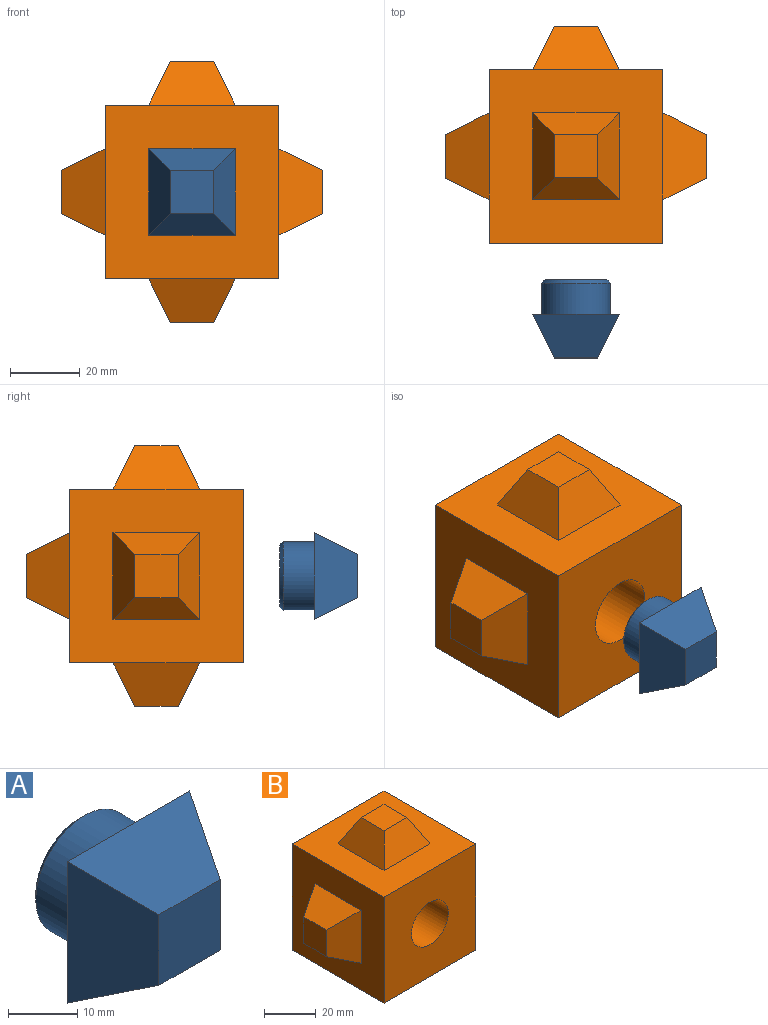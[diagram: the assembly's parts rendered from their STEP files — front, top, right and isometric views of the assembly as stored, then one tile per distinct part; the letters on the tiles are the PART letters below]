
ASSEMBLY  parts=2 mates=1
PART A: 16 faces, bbox 25x22.5x25 mm
  f0: plane 25x25mm, normal (0,1,0), area 317.1mm2, adj f2,f3,f4,f5,f6
  f1: plane 12.5x12.5mm, normal (0,-1,0), area 156.3mm2, adj f2,f3,f4,f5
  f2: plane 25x12.5mm, normal (0,-0.45,-0.89), area 262mm2, adj f0,f1,f3,f5
  f3: plane 25x12.5mm, normal (0.89,-0.45,0), area 262mm2, adj f0,f1,f2,f4
  f4: plane 25x12.5mm, normal (0,-0.45,0.89), area 262mm2, adj f0,f1,f3,f5
  f5: plane 25x12.5mm, normal (-0.89,-0.45,0), area 262mm2, adj f0,f1,f2,f4
  f6: cylinder r=9.9mm len=19.8mm, axis (0,-1,0), area 559.8mm2, adj f0,f15
  f7: plane 17.8x17.8mm, normal (0,1,0), area 76.8mm2, adj f14,f15
  f8: plane 16.91x16.91mm, normal (0,-1,0), area 113.9mm2, adj f10,f11,f12,f13,f14
  f9: plane 9.41x9.41mm, normal (0,1,0), area 88.5mm2, adj f10,f11,f12,f13
  f10: plane 16.91x7.5mm, normal (0,0.45,0.89), area 110.3mm2, adj f8,f9,f11,f13
  f11: plane 16.91x7.5mm, normal (-0.89,0.45,0), area 110.3mm2, adj f8,f9,f10,f12
  f12: plane 16.91x7.5mm, normal (0,0.45,-0.89), area 110.3mm2, adj f8,f9,f11,f13
  f13: plane 16.91x7.5mm, normal (0.89,0.45,0), area 110.3mm2, adj f8,f9,f10,f12
  f14: cylinder r=7.4mm len=14.8mm, axis (0,-1,0), area 581.2mm2, adj f7,f8
  f15: cone r=8.9mm half-angle=45deg, axis (0,-1,0), area 83.5mm2, adj f6,f7
PART B: 33 faces, bbox 75x62.5x75 mm
  f0: plane 12.5x12.5mm, normal (-1,0,0), area 156.3mm2, adj f1,f2,f3,f4
  f1: plane 25x12.5mm, normal (-0.45,0,-0.89), area 262mm2, adj f0,f2,f4,f13
  f2: plane 25x12.5mm, normal (-0.45,-0.89,0), area 262mm2, adj f0,f1,f3,f13
  f3: plane 25x12.5mm, normal (-0.45,0,0.89), area 262mm2, adj f0,f2,f4,f13
  f4: plane 25x12.5mm, normal (-0.45,0.89,0), area 262mm2, adj f0,f1,f3,f13
  f5: plane 12.5x12.5mm, normal (0,0,1), area 156.3mm2, adj f6,f7,f8,f9
  f6: plane 25x12.5mm, normal (-0.89,0,0.45), area 262mm2, adj f5,f7,f9,f12
  f7: plane 25x12.5mm, normal (0,-0.89,0.45), area 262mm2, adj f5,f6,f8,f12
  f8: plane 25x12.5mm, normal (0.89,0,0.45), area 262mm2, adj f5,f7,f9,f12
  f9: plane 25x12.5mm, normal (0,0.89,0.45), area 262mm2, adj f5,f6,f8,f12
  f10: plane 50x50mm, normal (0,1,0), area 1875mm2, adj f11,f12,f13,f14,f27,f28,f29,f30
  f11: plane 50x50mm, normal (1,0,0), area 1875mm2, adj f10,f12,f14,f15,f23,f24,f25,f26
  f12: plane 50x50mm, normal (0,0,1), area 1875mm2, adj f6,f7,f8,f9,f10,f11,f13,f15
  f13: plane 50x50mm, normal (-1,0,0), area 1875mm2, adj f1,f2,f3,f4,f10,f12,f14,f15
  f14: plane 50x50mm, normal (0,0,-1), area 1875mm2, adj f10,f11,f13,f15,f18,f19,f20,f21
  f15: plane 50x50mm, normal (0,-1,0), area 2185.8mm2, adj f11,f12,f13,f14,f16
  f16: cylinder r=10mm len=50mm, axis (0,-1,0), area 3141.6mm2, adj f15,f32
  f17: plane 12.5x12.5mm, normal (0,0,-1), area 156.3mm2, adj f18,f19,f20,f21
  f18: plane 25x12.5mm, normal (0.89,0,-0.45), area 262mm2, adj f14,f17,f19,f21
  f19: plane 25x12.5mm, normal (0,-0.89,-0.45), area 262mm2, adj f14,f17,f18,f20
  f20: plane 25x12.5mm, normal (-0.89,0,-0.45), area 262mm2, adj f14,f17,f19,f21
  f21: plane 25x12.5mm, normal (0,0.89,-0.45), area 262mm2, adj f14,f17,f18,f20
  f22: plane 12.5x12.5mm, normal (1,0,0), area 156.3mm2, adj f23,f24,f25,f26
  f23: plane 25x12.5mm, normal (0.45,0,0.89), area 262mm2, adj f11,f22,f24,f26
  f24: plane 25x12.5mm, normal (0.45,-0.89,0), area 262mm2, adj f11,f22,f23,f25
  f25: plane 25x12.5mm, normal (0.45,0,-0.89), area 262mm2, adj f11,f22,f24,f26
  f26: plane 25x12.5mm, normal (0.45,0.89,0), area 262mm2, adj f11,f22,f23,f25
  f27: plane 25x12.5mm, normal (0.89,0.45,0), area 262mm2, adj f10,f28,f30,f31
  f28: plane 25x12.5mm, normal (0,0.45,0.89), area 262mm2, adj f10,f27,f29,f31
  f29: plane 25x12.5mm, normal (-0.89,0.45,0), area 262mm2, adj f10,f28,f30,f31
  f30: plane 25x12.5mm, normal (0,0.45,-0.89), area 262mm2, adj f10,f27,f29,f31
  f31: plane 12.5x12.5mm, normal (0,1,0), area 156.3mm2, adj f27,f28,f29,f30
  f32: plane 20x20mm, normal (0,-1,0), area 314.2mm2, adj f16
PLACE A t=(-13.82,26.35,-14.36)mm
PLACE B t=(37.68,46.79,-14.36)mm fixed
MATE slider B.f16 <-> A.f6  axis (0,-1,0) through (37.68,21.79,-14.36)mm
